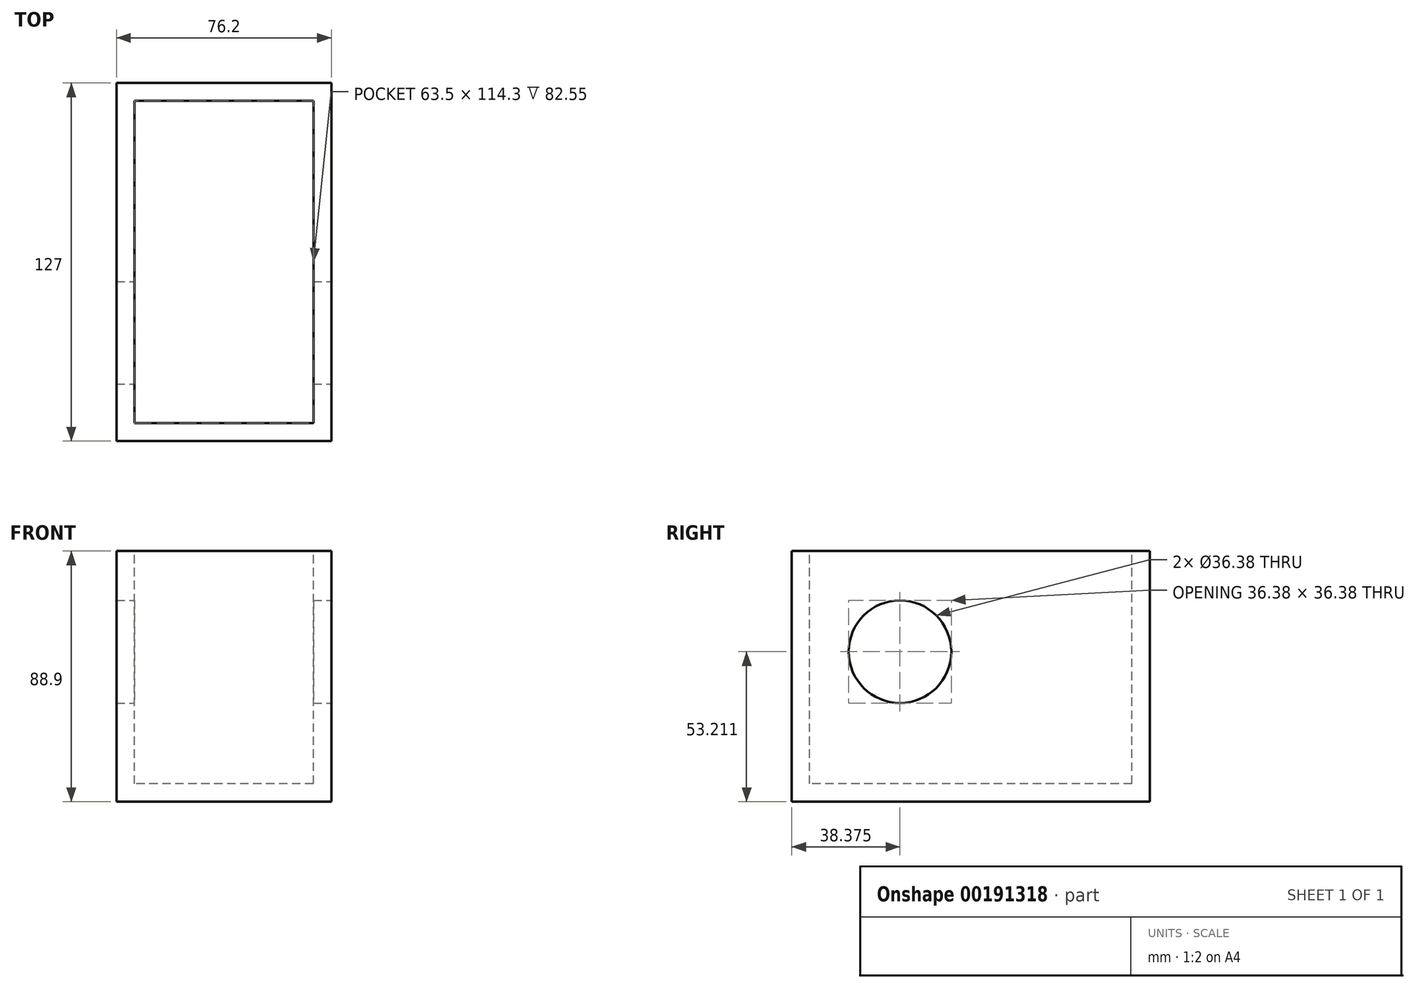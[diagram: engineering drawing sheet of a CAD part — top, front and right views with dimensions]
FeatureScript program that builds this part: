
annotation { "Feature Type Name" : "Feature", "Feature Type Description" : "" }
export const myFeature = defineFeature(function(context is Context, id is Id, definition is map)
    precondition{}
    {
        {
            var Q0;
            Q0=qCreatedBy(makeId("Top.planeOp"),FACE);
            var sketch = newSketch(context, id + "F0", { "sketchPlane" : qUnion([Q0])});
            skLineSegment(sketch, "E0.bottom", {"start": v(38.1, 63.5) * mm, "end": v(-38.1, 63.5) * mm});
            skLineSegment(sketch, "E0.top", {"start": v(38.1, -63.5) * mm, "end": v(-38.1, -63.5) * mm});
            skLineSegment(sketch, "E0.left", {"start": v(38.1, 63.5) * mm, "end": v(38.1, -63.5) * mm});
            skLineSegment(sketch, "E0.right", {"start": v(-38.1, 63.5) * mm, "end": v(-38.1, -63.5) * mm});
            skPoint(sketch, "E0.middle", {"position": v(0, 0) * mm});
            skSolve(sketch);
        }
        {
            var Q0;
            Q0 = qSketchRegion(id + "F0", true);
            extrude(context, id + "F1", {"entities" : qUnion([Q0]), "depth" : 88.9 * mm});
        }
        {
            var Q0;
            Q0=makeQuery(id+"F1.opExtrude","CAP_FACE",FACE,{"disambiguationData":[OSD([sQuery(id+"F0.wireOp",EDGE,"E0.bottom"),sQuery(id+"F0.wireOp",EDGE,"E0.top"),sQuery(id+"F0.wireOp",EDGE,"E0.left"),sQuery(id+"F0.wireOp",EDGE,"E0.right")])],"isStart":false});
            var sketch = newSketch(context, id + "F2", { "sketchPlane" : qUnion([Q0])});
            skLineSegment(sketch, "E1.bottom", {"start": v(31.75, 57.15) * mm, "end": v(-31.75, 57.15) * mm});
            skLineSegment(sketch, "E1.top", {"start": v(31.75, -57.15) * mm, "end": v(-31.75, -57.15) * mm});
            skLineSegment(sketch, "E1.left", {"start": v(31.75, 57.15) * mm, "end": v(31.75, -57.15) * mm});
            skLineSegment(sketch, "E1.right", {"start": v(-31.75, 57.15) * mm, "end": v(-31.75, -57.15) * mm});
            skPoint(sketch, "E1.middle", {"position": v(0, 0) * mm});
            skSolve(sketch);
        }
        {
            var Q0;
            Q0=makeQuery(id+"F2.imprint","IMPRINT",FACE,{"disambiguationData":[TD([[makeQuery(id+"F2.imprint","IMPRINT",EDGE,{"derivedFrom":sQuery(id+"F2.wireOp",EDGE,"E1.bottom")}),1.0]])]});
            extrude(context, id + "F3", {"entities" : qUnion([Q0]), "operationType" : NewBodyOperationType.REMOVE, "oppositeDirection" : true, "depth" : 82.55 * mm});
        }
        {
            var Q0;
            Q0=makeQuery(id+"F1.opExtrude","SWEPT_FACE",FACE,{"disambiguationData":[OSD([sQuery(id+"F0.wireOp",EDGE,"E0.left")])]});
            var sketch = newSketch(context, id + "F4", { "sketchPlane" : qUnion([Q0])});
            skCircle(sketch, "E2", {"center": v(-25.13, 53.21) * mm, "radius": 18.2 * mm});
            skSolve(sketch);
        }
        {
            var Q0;
            Q0=makeQuery(id+"F4.imprint","IMPRINT",FACE,{"disambiguationData":[TD([[makeQuery(id+"F4.imprint","IMPRINT",EDGE,{"derivedFrom":sQuery(id+"F4.wireOp",EDGE,"E2")}),1.0]])]});
            var Q1;
            Q1=sQuery(id+"F4.wireOp",EDGE,"E2");
            extrude(context, id + "F5", {"entities" : qUnion([Q0]), "operationType" : NewBodyOperationType.REMOVE, "surfaceEntities" : qUnion([Q1]), "endBound" : BoundingType.THROUGH_ALL, "oppositeDirection" : true, "depth" : 25.4 * mm});
        }
    });
